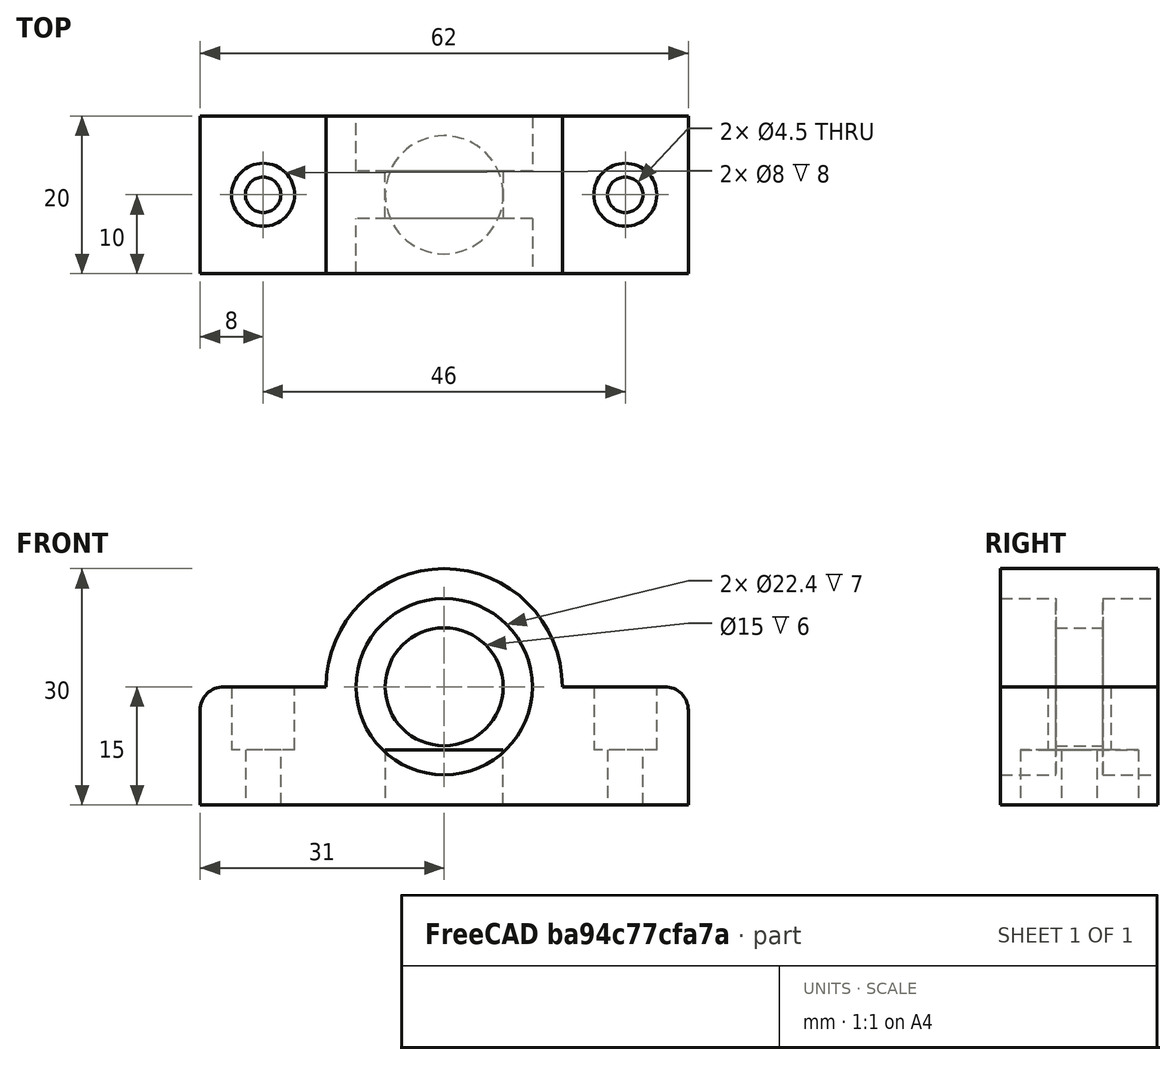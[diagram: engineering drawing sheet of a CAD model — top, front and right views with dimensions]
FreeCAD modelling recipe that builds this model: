
FCSTD DOCUMENT  (FreeCAD 1.0R1.0rc2)
Label: FlangeBearingA_RoadWheels
License: All rights reserved
LicenseURL: http://en.wikipedia.org/wiki/All_rights_reserved
objects: Part::Cylinder×9, Part::MultiFuse×5, Spreadsheet::Sheet×1, Part::Box×1, Part::Cut×1, Part::Fillet×1
note: 17 computed .brp shape members not serialized (recipe doc carries the construction recipe); baked Part::Feature solids carry a one-line shape summary decoded from their .brp

FEATURE [Spreadsheet::Sheet] Spreadsheet  label="BearingFlangeParameters"
  cells = A2='Bearing configuration; A3='Bearing OD; B3(bearing_od)=22; A4='Bearing thickness; B4(bearing_h)=7; A5='Tolerance; B5(tolerance)=0.2; A6='Bearing ID; B6(bearing_id)=15; A7='Base Profile configuration; A8='Width; B8(profile_width)=20; A9='Screw through dia; B9(screw_hole_dia)=4.5; A10='Bearing offset; B10(bearing_offset)=15; C10='This is the offset of the axis center from the profile base; A11='Min wall width; B11(min_wall_width)=4; C11='Wall width except for bearing offset towards profile; A12='Screw head dia; B12(screw_head_dia)=8; C12='M4 has 7mm diameter, leaving space; A13='Screw head height; B13(screw_head_height)=8; C13='M4 has 4mm, leaving space (and with +3mm can use 12mm screws)
FEATURE [Part::Cylinder] Cylinder
  Angle = 360
  AttacherType = Attacher::AttachEngine3D
  FirstAngle = 0
  Height = 7
  Placement = pos=(0,-3,15) rot=(1,0,0;1.5708rad)
  Radius = 11.2
  SecondAngle = 0
  expr: .Placement.Base.y = <<BearingFlangeParameters>>.bearing_h - <<BearingFlangeParameters>>.profile_width / 2
  expr: .Placement.Base.z = <<BearingFlangeParameters>>.bearing_offset
  expr: Height = <<BearingFlangeParameters>>.bearing_h
  expr: Radius = <<BearingFlangeParameters>>.bearing_od / 2 + <<BearingFlangeParameters>>.tolerance
FEATURE [Part::Cylinder] Cylinder001
  Angle = 360
  AttacherType = Attacher::AttachEngine3D
  FirstAngle = 0
  Height = 7
  Radius = 7.5
  SecondAngle = 0
  expr: Height = <<BearingFlangeParameters>>.bearing_h
  expr: Radius = <<BearingFlangeParameters>>.bearing_id / 2
FEATURE [Part::Cylinder] Cylinder002
  Angle = 360
  AttacherType = Attacher::AttachEngine3D
  FirstAngle = 0
  Height = 7
  Placement = pos=(0,10,15) rot=(1,0,0;1.5708rad)
  Radius = 11.2
  SecondAngle = 0
  expr: .Placement.Base.y = <<BearingFlangeParameters>>.profile_width / 2
  expr: .Placement.Base.z = <<BearingFlangeParameters>>.bearing_offset
  expr: Height = <<BearingFlangeParameters>>.bearing_h
  expr: Radius = <<BearingFlangeParameters>>.bearing_od / 2 + <<BearingFlangeParameters>>.tolerance
FEATURE [Part::Cylinder] Cylinder003
  Angle = 360
  AttacherType = Attacher::AttachEngine3D
  FirstAngle = 0
  Height = 20
  Placement = pos=(0,10,15) rot=(1,0,0;1.5708rad)
  Radius = 15
  SecondAngle = 0
  expr: .Placement.Base.y = <<BearingFlangeParameters>>.profile_width / 2
  expr: .Placement.Base.z = <<BearingFlangeParameters>>.bearing_offset
  expr: Height = <<BearingFlangeParameters>>.profile_width
  expr: Radius = <<BearingFlangeParameters>>.bearing_od / 2 + <<BearingFlangeParameters>>.min_wall_width
FEATURE [Part::Cylinder] Cylinder004
  Angle = 360
  AttacherType = Attacher::AttachEngine3D
  FirstAngle = 0
  Height = 20
  Placement = pos=(0,10,15) rot=(1,0,0;1.5708rad)
  Radius = 7.5
  SecondAngle = 0
  expr: .Placement.Base.y = <<BearingFlangeParameters>>.profile_width / 2
  expr: .Placement.Base.z = <<BearingFlangeParameters>>.bearing_offset
  expr: Height = <<BearingFlangeParameters>>.profile_width
  expr: Radius = <<BearingFlangeParameters>>.bearing_id / 2
FEATURE [Part::MultiFuse] Fusion
  Shapes = -> [Cylinder004,Cylinder,Cylinder002]
FEATURE [Part::Box] Box001  label="Cube001"
  AttacherType = Attacher::AttachEngine3D
  Height = 15
  Length = 62
  Placement = pos=(-31,-10,0) rot=(0,0,1;0rad)
  Width = 20
  expr: .Placement.Base.x = -(4 * <<BearingFlangeParameters>>.min_wall_width + 2 * <<BearingFlangeParameters>>.screw_head_dia + 2 * (<<BearingFlangeParameters>>.bearing_od / 2 + <<BearingFlangeParameters>>.min_wall_width)) / 2
  expr: .Placement.Base.y = -<<BearingFlangeParameters>>.profile_width / 2
  expr: Height = <<BearingFlangeParameters>>.bearing_od / 2 + <<BearingFlangeParameters>>.min_wall_width
  expr: Length = 4 * <<BearingFlangeParameters>>.min_wall_width + 2 * <<BearingFlangeParameters>>.screw_head_dia + 2 * (<<BearingFlangeParameters>>.bearing_od / 2 + <<BearingFlangeParameters>>.min_wall_width)
  expr: Width = <<BearingFlangeParameters>>.profile_width
FEATURE [Part::Cylinder] Cylinder005
  Angle = 360
  AttacherType = Attacher::AttachEngine3D
  FirstAngle = 0
  Height = 15
  Radius = 2.25
  SecondAngle = 0
  expr: Height = <<BearingFlangeParameters>>.bearing_od / 2 + <<BearingFlangeParameters>>.min_wall_width
  expr: Radius = <<BearingFlangeParameters>>.screw_hole_dia / 2
FEATURE [Part::Cylinder] Cylinder006
  Angle = 360
  AttacherType = Attacher::AttachEngine3D
  FirstAngle = 0
  Height = 8
  Placement = pos=(0,0,7) rot=(0,0,1;0rad)
  Radius = 4
  SecondAngle = 0
  expr: .Placement.Base.z = <<BearingFlangeParameters>>.bearing_od / 2 + <<BearingFlangeParameters>>.min_wall_width - <<BearingFlangeParameters>>.screw_head_height
  expr: Height = <<BearingFlangeParameters>>.screw_head_height
  expr: Radius = <<BearingFlangeParameters>>.screw_head_dia / 2
FEATURE [Part::MultiFuse] Fusion001
  Placement = pos=(23,0,0) rot=(0,0,1;0rad)
  Shapes = -> [Cylinder005,Cylinder006]
  expr: .Placement.Base.x = <<BearingFlangeParameters>>.bearing_od / 2 + <<BearingFlangeParameters>>.min_wall_width + <<BearingFlangeParameters>>.min_wall_width + <<BearingFlangeParameters>>.screw_head_dia / 2
FEATURE [Part::Cylinder] Cylinder007
  Angle = 360
  AttacherType = Attacher::AttachEngine3D
  FirstAngle = 0
  Height = 15
  Radius = 2.25
  SecondAngle = 0
  expr: Height = <<BearingFlangeParameters>>.bearing_od / 2 + <<BearingFlangeParameters>>.min_wall_width
  expr: Radius = <<BearingFlangeParameters>>.screw_hole_dia / 2
FEATURE [Part::Cylinder] Cylinder008
  Angle = 360
  AttacherType = Attacher::AttachEngine3D
  FirstAngle = 0
  Height = 8
  Placement = pos=(0,0,7) rot=(0,0,1;0rad)
  Radius = 4
  SecondAngle = 0
  expr: .Placement.Base.z = <<BearingFlangeParameters>>.bearing_od / 2 + <<BearingFlangeParameters>>.min_wall_width - <<BearingFlangeParameters>>.screw_head_height
  expr: Height = <<BearingFlangeParameters>>.screw_head_height
  expr: Radius = <<BearingFlangeParameters>>.screw_head_dia / 2
FEATURE [Part::MultiFuse] Fusion002
  Placement = pos=(-23,0,0) rot=(0,0,1;0rad)
  Shapes = -> [Cylinder007,Cylinder008]
  expr: .Placement.Base.x = -1 * (<<BearingFlangeParameters>>.bearing_od / 2 + <<BearingFlangeParameters>>.min_wall_width + <<BearingFlangeParameters>>.min_wall_width + <<BearingFlangeParameters>>.screw_head_dia / 2)
FEATURE [Part::MultiFuse] Fusion003
  Shapes = -> [Fusion001,Fusion002,Fusion]
FEATURE [Part::MultiFuse] Fusion004
  Shapes = -> [Box001,Cylinder003]
FEATURE [Part::Cut] Cut
  Base = -> Fusion004
  Tool = -> Fusion003
FEATURE [Part::Fillet] Fillet
  Base = -> Cut
  EdgeLinks = -> Cut [Edge2,Edge41]
  Edges = 2 edges r=3: [Edge2,Edge41]
